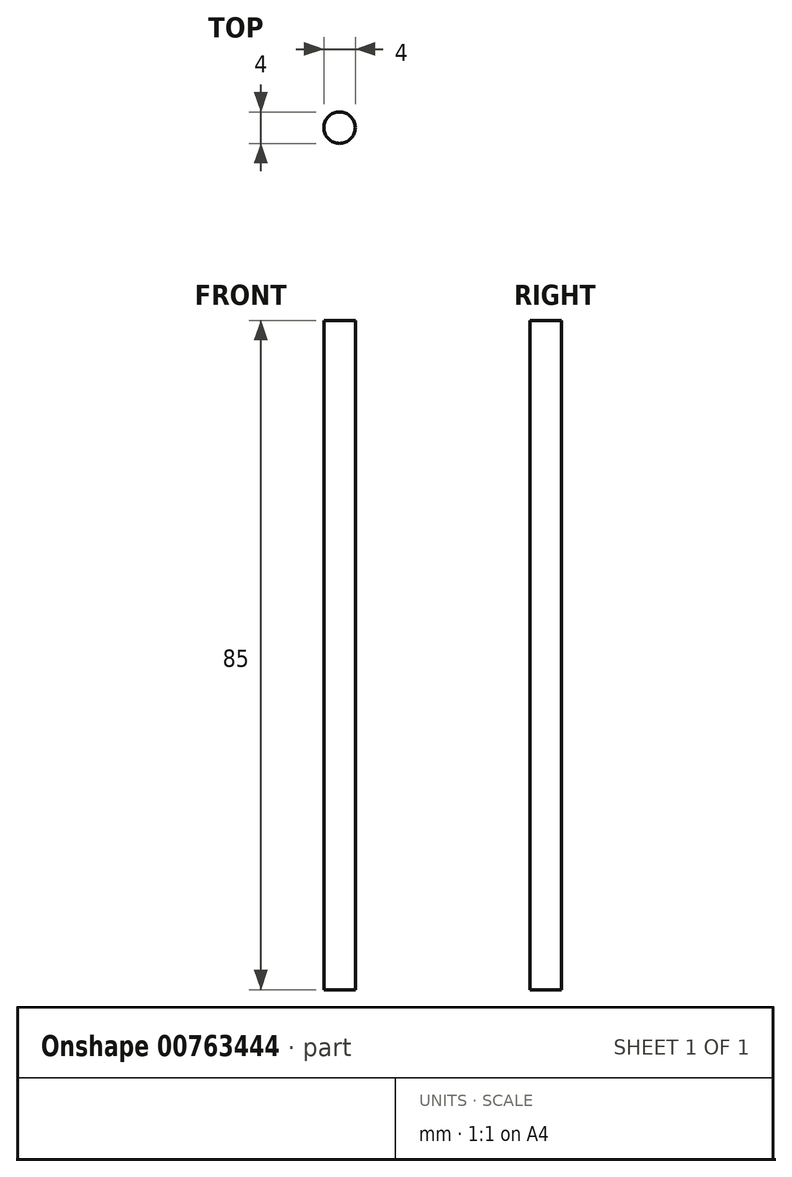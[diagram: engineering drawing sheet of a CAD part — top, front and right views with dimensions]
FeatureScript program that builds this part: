
annotation { "Feature Type Name" : "Feature", "Feature Type Description" : "" }
export const myFeature = defineFeature(function(context is Context, id is Id, definition is map)
    precondition{}
    {
        {
            var Q0;
            Q0=qCreatedBy(makeId("Top.planeOp"),FACE);
            var sketch = newSketch(context, id + "F0", { "sketchPlane" : qUnion([Q0])});
            skCircle(sketch, "E0", {"center": v(0, 0) * mm, "radius": 2 * mm});
            skSolve(sketch);
        }
        {
            var Q0;
            Q0 = qSketchRegion(id + "F0", true);
            extrude(context, id + "F1", {"entities" : qUnion([Q0]), "depth" : 85 * mm, "offsetDistance" : 25 * mm});
        }
    });
